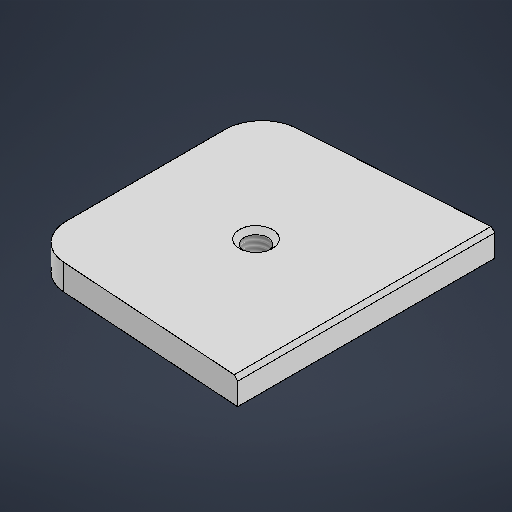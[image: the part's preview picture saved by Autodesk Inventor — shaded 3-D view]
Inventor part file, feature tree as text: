
AUTODESK INVENTOR PART (.ipt)
format: ipt  version: 2025.3 (Build 293356000, 356)  size: 196,608 bytes
history: native  units: mm
features: chamfer x2, sketch x1, extrude x1, hole x1, fillet x1
ambient origin geometry x8: Origin, YZ Plane, XZ Plane, XY Plane, X Axis, Y Axis, Z Axis, Center Point
bodies: Solid1 (feature_tree)
feature tree (6):
  sketch  "Sketch1"  dims[d1=30.0mm d2=35.0mm d3=4.0mm d4=0.0mm d5=3.242mm d6=8.0mm d7=4.5mm d8=6.8mm d9=90.0deg d10=8.0mm d11=20.594885mm d12=0.25mm d13=2.0mm d14=45.0deg d15=5.0mm d16=0.5mm d17=2.0mm d18=45.0deg d19=31.0mm d20=30.0mm]
  extrude  "Extrusion1"  Depth=30.0mm
  hole  "Hole1"  [1 undecoded]
  chamfer  "Chamfer1"  Distance=0.25mm Angle=45.0deg
  fillet  "Fillet1"  Radius=5.0mm
  chamfer  "Chamfer2"  Distance=0.5mm Angle=45.0deg
note: 1 required parameter value undecoded (feature->parameter linkage not recoverable at this tier; creation-order binding heuristic only, values carry confidence <= 0.55)
